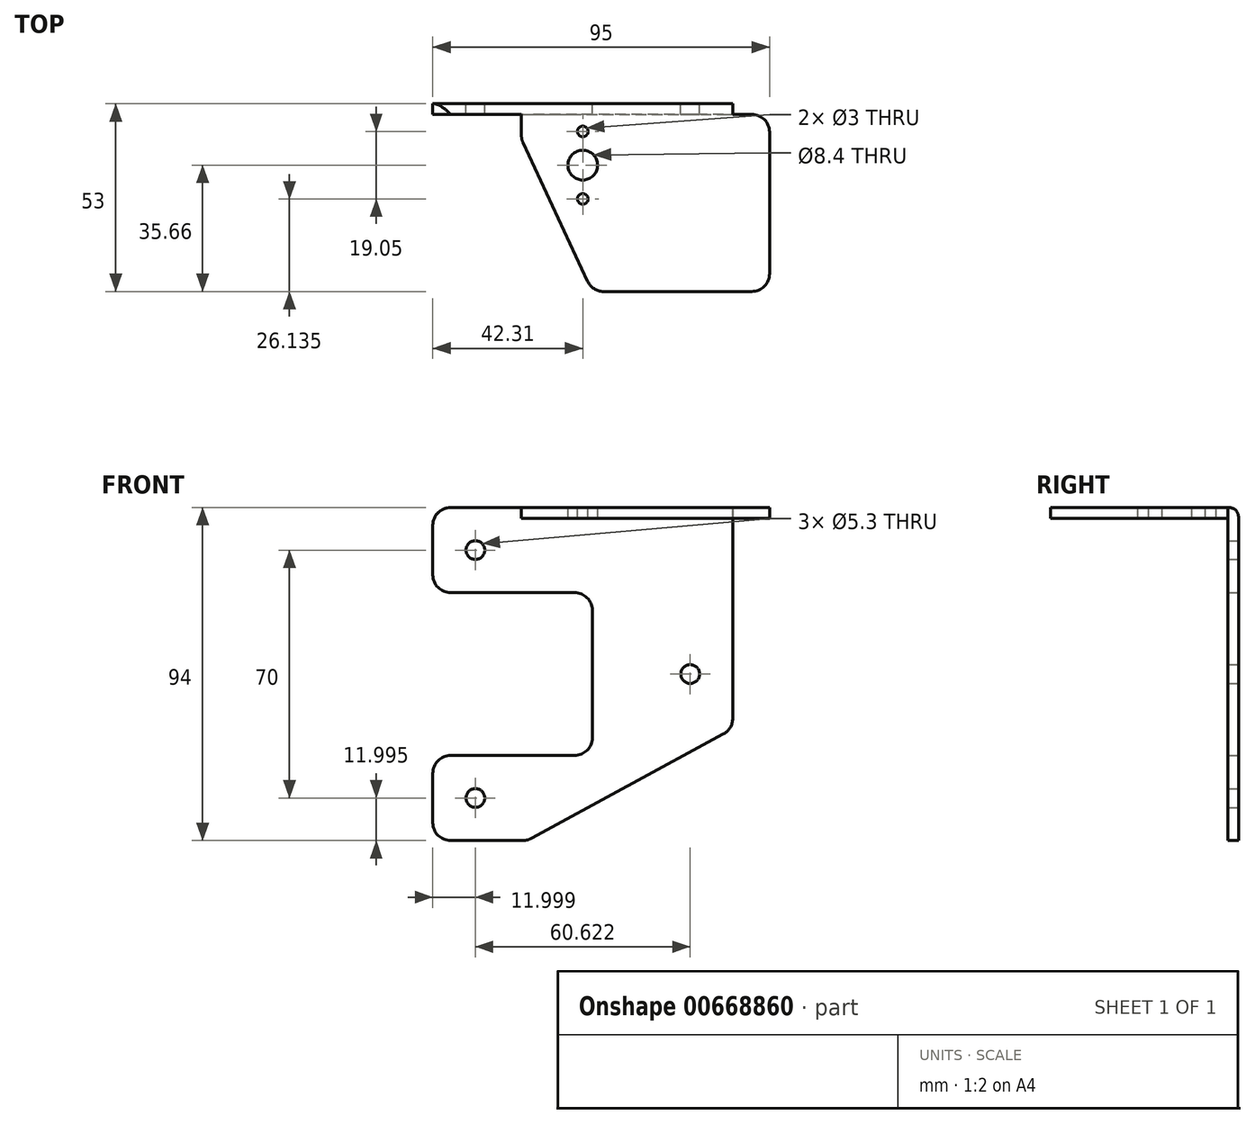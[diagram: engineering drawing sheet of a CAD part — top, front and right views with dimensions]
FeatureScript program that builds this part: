
annotation { "Feature Type Name" : "Feature", "Feature Type Description" : "" }
export const myFeature = defineFeature(function(context is Context, id is Id, definition is map)
    precondition{}
    {
        {
            var Q0;
            Q0=qCreatedBy(makeId("Front.planeOp"),FACE);
            var sketch = newSketch(context, id + "F0", { "sketchPlane" : qUnion([Q0])});
            skCircle(sketch, "E0", {"center": v(-38.66, 36.84) * mm, "radius": 2.65 * mm});
            skCircle(sketch, "E1", {"center": v(-38.66, -33.16) * mm, "radius": 2.65 * mm});
            skCircle(sketch, "E2", {"center": v(21.96, 1.84) * mm, "radius": 2.65 * mm});
            skLineSegment(sketch, "E3", {"start": v(-47.63, 48.84) * mm, "end": v(33.96, 48.84) * mm});
            skLineSegment(sketch, "E4", {"start": v(33.96, 48.84) * mm, "end": v(33.96, -13.67) * mm});
            skLineSegment(sketch, "E5", {"start": v(33.96, -13.67) * mm, "end": v(-23.95, -45.16) * mm});
            skLineSegment(sketch, "E6", {"start": v(-23.95, -45.16) * mm, "end": v(-50.66, -45.16) * mm});
            skLineSegment(sketch, "E7", {"start": v(-50.66, -45.16) * mm, "end": v(-50.66, 48.84) * mm});
            skLineSegment(sketch, "E8", {"start": v(-50.66, 48.84) * mm, "end": v(-47.63, 48.84) * mm});
            skLineSegment(sketch, "E9.bottom", {"start": v(-50.66, 24.84) * mm, "end": v(-5.66, 24.84) * mm});
            skLineSegment(sketch, "E9.top", {"start": v(-50.66, -21.16) * mm, "end": v(-5.66, -21.16) * mm});
            skLineSegment(sketch, "E9.left", {"start": v(-50.66, 24.84) * mm, "end": v(-50.66, -21.16) * mm});
            skLineSegment(sketch, "E9.right", {"start": v(-5.66, 24.84) * mm, "end": v(-5.66, -21.16) * mm});
            skLineSegment(sketch, "E10.bottom", {"start": v(11.65, 30.07) * mm, "end": v(-28.35, 30.07) * mm});
            skLineSegment(sketch, "E10.top", {"start": v(11.65, -24) * mm, "end": v(-28.35, -24) * mm});
            skLineSegment(sketch, "E10.left", {"start": v(11.65, 30.07) * mm, "end": v(11.65, -24) * mm});
            skLineSegment(sketch, "E10.right", {"start": v(-28.35, 30.07) * mm, "end": v(-28.35, -24) * mm});
            skSolve(sketch);
        }
        {
            var Q0;
            Q0=makeQuery(id+"F0.imprint","IMPRINT",FACE,{"disambiguationData":[TD([[makeQuery(id+"F0.imprint","IMPRINT",EDGE,{"derivedFrom":sQuery(id+"F0.wireOp",EDGE,"E0")}),-1.0]])]});
            var Q1;
            Q1=makeQuery(id+"F0.imprint","IMPRINT",FACE,{"disambiguationData":[TD([[makeQuery(id+"F0.imprint","IMPRINT",EDGE,{"derivedFrom":sQuery(id+"F0.wireOp",EDGE,"E2")}),-1.0]])]});
            var Q2;
            {var subQ0=sQuery(id+"F0.wireOp",EDGE,"E9.right");Q2=makeQuery(id+"F0.imprint","IMPRINT",FACE,{"disambiguationData":[TD([[makeQuery(id+"F0.imprint","IMPRINT",EDGE,{"derivedFrom":subQ0}),1.0]])]});}
            var Q3;
            Q3=makeQuery(id+"F0.imprint","IMPRINT",FACE,{"disambiguationData":[TD([[makeQuery(id+"F0.imprint","IMPRINT",EDGE,{"derivedFrom":sQuery(id+"F0.wireOp",EDGE,"E1")}),-1.0]])]});
            extrude(context, id + "F1", {"entities" : qUnion([Q0, Q1, Q2, Q3]), "depth" : 3 * mm, "offsetDistance" : 25 * mm});
        }
        {
            var Q0;
            Q0=makeQuery(id+"F1.opExtrude","CAP_FACE",FACE,{"disambiguationData":[OSD([sQuery(id+"F0.wireOp",EDGE,"E0"),sQuery(id+"F0.wireOp",EDGE,"E1"),sQuery(id+"F0.wireOp",EDGE,"E2"),sQuery(id+"F0.wireOp",EDGE,"E3"),sQuery(id+"F0.wireOp",EDGE,"E4"),sQuery(id+"F0.wireOp",EDGE,"E5"),sQuery(id+"F0.wireOp",EDGE,"E6"),sQuery(id+"F0.wireOp",EDGE,"E7"),sQuery(id+"F0.wireOp",EDGE,"E8"),sQuery(id+"F0.wireOp",EDGE,"E9.bottom"),sQuery(id+"F0.wireOp",EDGE,"E9.top"),sQuery(id+"F0.wireOp",EDGE,"E9.right")])],"isStart":false});
            var sketch = newSketch(context, id + "F2", { "sketchPlane" : qUnion([Q0])});
            skLineSegment(sketch, "E11.bottom", {"start": v(-25.66, 48.84) * mm, "end": v(44.34, 48.84) * mm});
            skLineSegment(sketch, "E11.top", {"start": v(-25.66, 45.84) * mm, "end": v(44.34, 45.84) * mm});
            skLineSegment(sketch, "E11.left", {"start": v(-25.66, 48.84) * mm, "end": v(-25.66, 45.84) * mm});
            skLineSegment(sketch, "E11.right", {"start": v(44.34, 48.84) * mm, "end": v(44.34, 45.84) * mm});
            skSolve(sketch);
        }
        {
            var Q0;
            Q0=makeQuery(id+"F2.imprint","IMPRINT",FACE,{"disambiguationData":[TD([[makeQuery(id+"F2.imprint","IMPRINT",EDGE,{"derivedFrom":sQuery(id+"F2.wireOp",EDGE,"E11.bottom")}),-1.0]])]});
            extrude(context, id + "F3", {"entities" : qUnion([Q0]), "operationType" : NewBodyOperationType.ADD, "depth" : 50 * mm, "offsetDistance" : 25 * mm});
        }
        {
            var Q0;
            Q0=makeQuery(id+"F3.opExtrude","CAP_EDGE",EDGE,{"disambiguationData":[OSD([sQuery(id+"F2.wireOp",EDGE,"E11.left")])],"isStart":false});
            chamfer(context, id + "F4", {"entities" : qUnion([Q0]), "chamferType" : ChamferType.TWO_OFFSETS, "width1" : 20 * mm, "oppositeDirection" : false, "width2" : 43 * mm, "tangentPropagation" : true});
        }
        {
            var Q0;
            {var subQ0=sQuery(id+"F2.wireOp",EDGE,"E11.left");Q0=makeQuery(id+"F4.opChamfer","BLEND_EDGE",EDGE,{"blendedFrom":[makeQuery(id+"F3.opExtrude","CAP_EDGE",EDGE,{"disambiguationData":[OSD([subQ0])],"isStart":false}),makeQuery(id+"F3.opExtrude","CAP_FACE",FACE,{"disambiguationData":[OSD([sQuery(id+"F2.wireOp",EDGE,"E11.bottom"),sQuery(id+"F2.wireOp",EDGE,"E11.top"),subQ0,sQuery(id+"F2.wireOp",EDGE,"E11.right")])],"isStart":false})],"blendedInto":[makeQuery(id+"F3.opExtrude","CAP_FACE",FACE,{"disambiguationData":[OSD([sQuery(id+"F2.wireOp",EDGE,"E11.bottom"),sQuery(id+"F2.wireOp",EDGE,"E11.top"),subQ0,sQuery(id+"F2.wireOp",EDGE,"E11.right")])],"isStart":false})]});}
            fillet(context, id + "F5", {"entities" : qUnion([Q0]), "radius" : 5 * mm, "tangentPropagation" : true, "allowEdgeOverflow" : false});
        }
        {
            var Q0;
            {var subQ0=sQuery(id+"F2.wireOp",EDGE,"E11.left");Q0=makeQuery(id+"F4.opChamfer","BLEND_EDGE",EDGE,{"blendedFrom":[makeQuery(id+"F3.opExtrude","CAP_EDGE",EDGE,{"disambiguationData":[OSD([subQ0])],"isStart":false}),makeQuery(id+"F3.opExtrude","SWEPT_FACE",FACE,{"disambiguationData":[OSD([subQ0])]})],"blendedInto":[makeQuery(id+"F3.opExtrude","SWEPT_FACE",FACE,{"disambiguationData":[OSD([subQ0])]})]});}
            fillet(context, id + "F6", {"entities" : qUnion([Q0]), "radius" : 5 * mm, "tangentPropagation" : true, "allowEdgeOverflow" : false});
        }
        {
            var Q0;
            Q0=makeQuery(id+"F3.opExtrude","CAP_EDGE",EDGE,{"disambiguationData":[OSD([sQuery(id+"F2.wireOp",EDGE,"E11.right")])],"isStart":false});
            fillet(context, id + "F7", {"entities" : qUnion([Q0]), "radius" : 5 * mm, "tangentPropagation" : true, "allowEdgeOverflow" : false});
        }
        {
            var Q0;
            Q0=makeQuery(id+"F1.opExtrude","SWEPT_EDGE",EDGE,{"disambiguationData":[OSD([sQuery(id+"F0.wireOp",EDGE,"E7"),sQuery(id+"F0.wireOp",EDGE,"E9.bottom"),sQuery(id+"F0.wireOp",EDGE,"E9.left")])]});
            var Q1;
            Q1=makeQuery(id+"F1.opExtrude","SWEPT_EDGE",EDGE,{"disambiguationData":[OSD([sQuery(id+"F0.wireOp",EDGE,"E7"),sQuery(id+"F0.wireOp",EDGE,"E8")])]});
            var Q2;
            Q2=makeQuery(id+"F1.opExtrude","SWEPT_EDGE",EDGE,{"disambiguationData":[OSD([sQuery(id+"F0.wireOp",EDGE,"E9.top"),sQuery(id+"F0.wireOp",EDGE,"E9.right")])]});
            var Q3;
            Q3=makeQuery(id+"F1.opExtrude","SWEPT_EDGE",EDGE,{"disambiguationData":[OSD([sQuery(id+"F0.wireOp",EDGE,"E7"),sQuery(id+"F0.wireOp",EDGE,"E9.top"),sQuery(id+"F0.wireOp",EDGE,"E9.left")])]});
            var Q4;
            Q4=makeQuery(id+"F1.opExtrude","SWEPT_EDGE",EDGE,{"disambiguationData":[OSD([sQuery(id+"F0.wireOp",EDGE,"E6"),sQuery(id+"F0.wireOp",EDGE,"E7")])]});
            var Q5;
            Q5=makeQuery(id+"F1.opExtrude","SWEPT_EDGE",EDGE,{"disambiguationData":[OSD([sQuery(id+"F0.wireOp",EDGE,"E5"),sQuery(id+"F0.wireOp",EDGE,"E6")])]});
            var Q6;
            Q6=makeQuery(id+"F1.opExtrude","SWEPT_EDGE",EDGE,{"disambiguationData":[OSD([sQuery(id+"F0.wireOp",EDGE,"E4"),sQuery(id+"F0.wireOp",EDGE,"E5")])]});
            var Q7;
            Q7=makeQuery(id+"F1.opExtrude","SWEPT_EDGE",EDGE,{"disambiguationData":[OSD([sQuery(id+"F0.wireOp",EDGE,"E9.bottom"),sQuery(id+"F0.wireOp",EDGE,"E9.right")])]});
            fillet(context, id + "F8", {"entities" : qUnion([Q0, Q1, Q2, Q3, Q4, Q5, Q6, Q7]), "radius" : 5 * mm, "tangentPropagation" : true, "allowEdgeOverflow" : false});
        }
        {
            var Q0;
            Q0=makeQuery(id+"F1.opExtrude","CAP_EDGE",EDGE,{"disambiguationData":[OSD([sQuery(id+"F0.wireOp",EDGE,"E3"),sQuery(id+"F0.wireOp",EDGE,"E8")])],"isStart":true});
            fillet(context, id + "F9", {"entities" : qUnion([Q0]), "radius" : 3 * mm, "rho" : 0.5, "crossSection" : FilletCrossSection.CONIC, "allowEdgeOverflow" : false});
        }
        {
            var Q0;
            Q0=makeQuery(id+"F3.boolean.opBoolean","MERGE",FACE,{"derivedFrom":[makeQuery(id+"F1.opExtrude","SWEPT_FACE",FACE,{"disambiguationData":[OSD([sQuery(id+"F0.wireOp",EDGE,"E3"),sQuery(id+"F0.wireOp",EDGE,"E8")])]}),makeQuery(id+"F3.opExtrude","SWEPT_FACE",FACE,{"disambiguationData":[OSD([sQuery(id+"F2.wireOp",EDGE,"E11.bottom")])]})]});
            var sketch = newSketch(context, id + "F10", { "sketchPlane" : qUnion([Q0])});
            skPoint(sketch, "E12", {"position": v(-39.35, -2.75) * mm});
            skCircle(sketch, "E13", {"center": v(-8.35, -7.82) * mm, "radius": 1.5 * mm});
            skCircle(sketch, "E14", {"center": v(-8.35, -26.86) * mm, "radius": 1.5 * mm});
            skPoint(sketch, "E15", {"position": v(-8.35, -3) * mm});
            skLineSegment(sketch, "E16.bottom", {"start": v(-29.35, 3.66) * mm, "end": v(12.65, 3.66) * mm});
            skLineSegment(sketch, "E16.top", {"start": v(-29.35, -38.34) * mm, "end": v(12.65, -38.34) * mm});
            skLineSegment(sketch, "E16.left", {"start": v(-29.35, 3.66) * mm, "end": v(-29.35, -38.34) * mm});
            skLineSegment(sketch, "E16.right", {"start": v(12.65, 3.66) * mm, "end": v(12.65, -38.34) * mm});
            skCircle(sketch, "E17", {"center": v(-8.35, -17.34) * mm, "radius": 12.7 * mm});
            skLineSegment(sketch, "E18.bottom", {"start": v(-28.35, 3.66) * mm, "end": v(11.65, 3.66) * mm});
            skLineSegment(sketch, "E18.top", {"start": v(-28.35, 23.66) * mm, "end": v(11.65, 23.66) * mm});
            skLineSegment(sketch, "E18.left", {"start": v(-28.35, 3.66) * mm, "end": v(-28.35, 23.66) * mm});
            skLineSegment(sketch, "E18.right", {"start": v(11.65, 3.66) * mm, "end": v(11.65, 23.66) * mm});
            skCircle(sketch, "E19", {"center": v(-8.35, -17.34) * mm, "radius": 6.35 * mm});
            skCircle(sketch, "E20", {"center": v(-8.35, -17.34) * mm, "radius": 4.2 * mm});
            skSolve(sketch);
        }
        {
            var Q0;
            Q0=makeQuery(id+"F10.imprint","IMPRINT",FACE,{"disambiguationData":[TD([[makeQuery(id+"F10.imprint","IMPRINT",EDGE,{"derivedFrom":sQuery(id+"F10.wireOp",EDGE,"E14")}),1.0]])]});
            var Q1;
            Q1=makeQuery(id+"F10.imprint","IMPRINT",FACE,{"disambiguationData":[TD([[makeQuery(id+"F10.imprint","IMPRINT",EDGE,{"derivedFrom":sQuery(id+"F10.wireOp",EDGE,"E13")}),1.0]])]});
            var Q2;
            Q2=makeQuery(id+"F3.opExtrude","SWEPT_FACE",FACE,{"disambiguationData":[OSD([sQuery(id+"F2.wireOp",EDGE,"E11.top")])]});
            extrude(context, id + "F11", {"entities" : qUnion([Q0, Q1]), "operationType" : NewBodyOperationType.REMOVE, "endBound" : BoundingType.UP_TO_SURFACE, "oppositeDirection" : true, "depth" : 7.3 * mm, "endBoundEntityFace" : qUnion([Q2]), "offsetDistance" : 25 * mm});
        }
        {
            var Q0;
            Q0=makeQuery(id+"F3.opExtrude","CAP_EDGE",EDGE,{"disambiguationData":[OSD([sQuery(id+"F2.wireOp",EDGE,"E11.right")])],"isStart":true});
            fillet(context, id + "F12", {"entities" : qUnion([Q0]), "radius" : 5 * mm, "tangentPropagation" : true, "allowEdgeOverflow" : false});
        }
        {
            var Q0;
            Q0=makeQuery(id+"F10.imprint","IMPRINT",FACE,{"disambiguationData":[TD([[makeQuery(id+"F10.imprint","IMPRINT",EDGE,{"derivedFrom":sQuery(id+"F10.wireOp",EDGE,"E20")}),1.0]])]});
            extrude(context, id + "F13", {"entities" : qUnion([Q0]), "operationType" : NewBodyOperationType.REMOVE, "oppositeDirection" : true, "depth" : 25 * mm, "offsetDistance" : 25 * mm});
        }
    });
